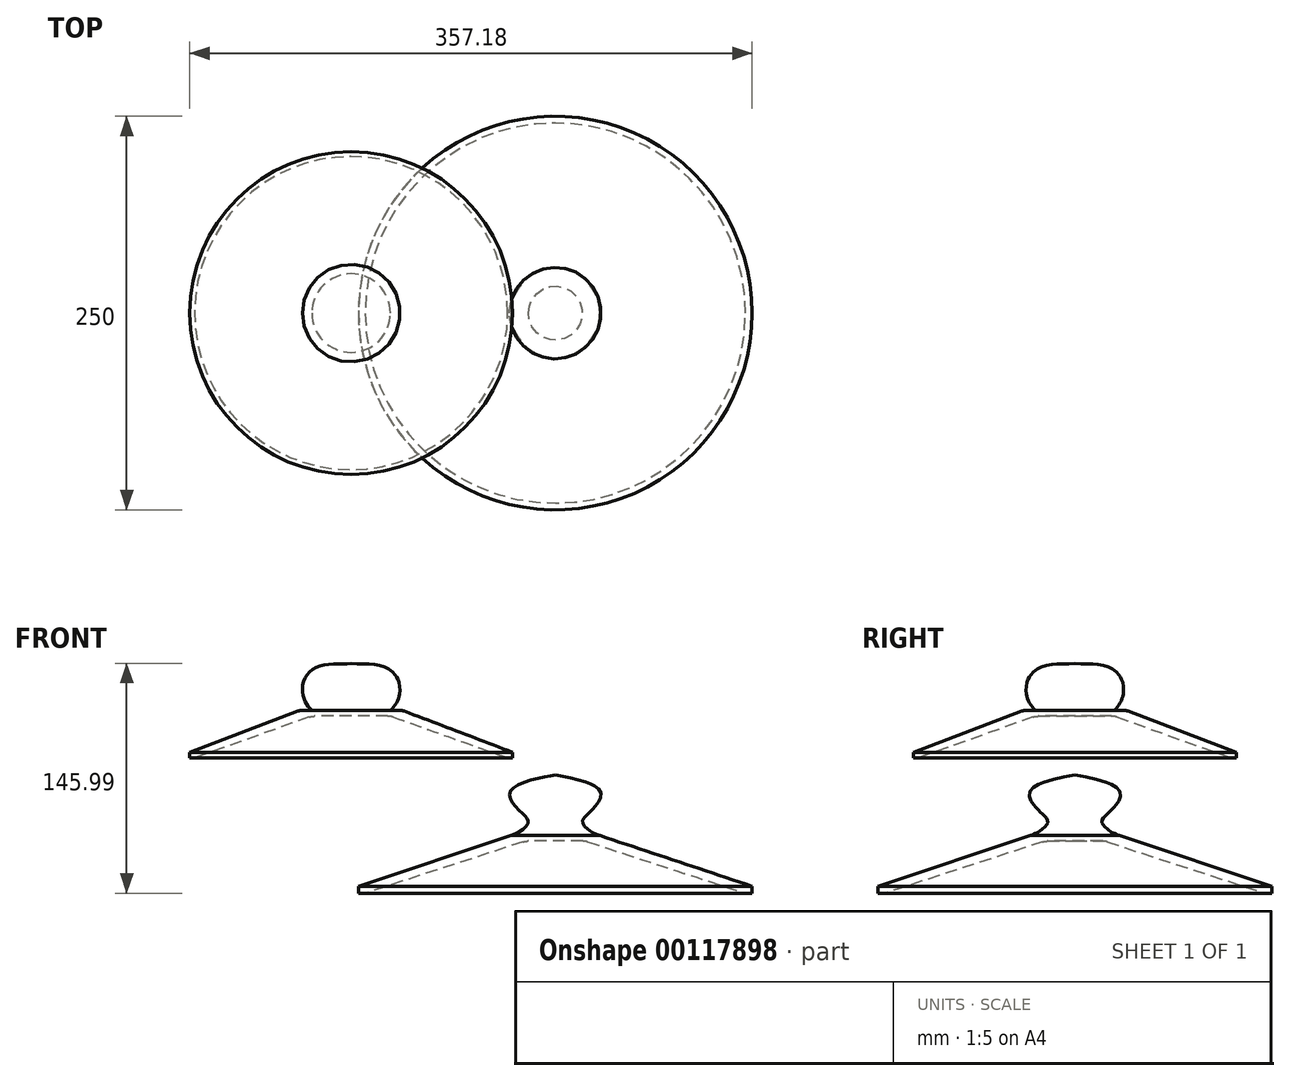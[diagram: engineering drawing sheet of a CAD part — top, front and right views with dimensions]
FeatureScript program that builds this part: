
annotation { "Feature Type Name" : "Feature", "Feature Type Description" : "" }
export const myFeature = defineFeature(function(context is Context, id is Id, definition is map)
    precondition{}
    {
        {
            var Q0;
            Q0=qCreatedBy(makeId("Front.planeOp"),FACE);
            var sketch = newSketch(context, id + "F0", { "sketchPlane" : qUnion([Q0])});
            skLineSegment(sketch, "E0.bottom", {"start": v(-58.02, 56.21) * mm, "end": v(44.48, 56.21) * mm});
            skLineSegment(sketch, "E0.top", {"start": v(-58.02, -3.79) * mm, "end": v(-54.94, -3.79) * mm});
            skLineSegment(sketch, "E0.left", {"start": v(-58.02, 56.21) * mm, "end": v(-58.02, 27.98) * mm});
            skLineSegment(sketch, "E0.right", {"start": v(44.48, 56.21) * mm, "end": v(44.48, 26.21) * mm});
            skLineSegment(sketch, "E1", {"start": v(-58.02, -0.25) * mm, "end": v(-58.02, -3.79) * mm});
            skLineSegment(sketch, "E2", {"start": v(-58.02, -0.25) * mm, "end": v(10.73, 25.88) * mm});
            skLineSegment(sketch, "E3", {"start": v(-54.94, -3.79) * mm, "end": v(44.48, -3.79) * mm});
            skLineSegment(sketch, "E4", {"start": v(-58.02, 27.98) * mm, "end": v(-58.02, -0.25) * mm});
            skLineSegment(sketch, "E5", {"start": v(44.48, 26.21) * mm, "end": v(44.48, 22.67) * mm});
            skLineSegment(sketch, "E6", {"start": v(44.48, 22.67) * mm, "end": v(44.48, -3.79) * mm});
            skLineSegment(sketch, "E7", {"start": v(12.5, 26.21) * mm, "end": v(19.51, 26.21) * mm});
            skLineSegment(sketch, "E8", {"start": v(44.48, 22.67) * mm, "end": v(21.24, 22.67) * mm});
            skLineSegment(sketch, "E9", {"start": v(17.89, 22.1) * mm, "end": v(-54.94, -3.79) * mm});
            skPoint(sketch, "E10.visualSharp", {"position": v(11.59, 26.21) * mm});
            skArc(sketch, "E10.filletArc", {"start": v(12.5, 26.21) * mm, "mid": v(11.6, 26.13) * mm, "end": v(10.73, 25.88) * mm});
            skPoint(sketch, "E11.visualSharp", {"position": v(19.51, 22.67) * mm});
            skArc(sketch, "E11.filletArc", {"start": v(21.24, 22.67) * mm, "mid": v(19.54, 22.53) * mm, "end": v(17.89, 22.1) * mm});
            skFitSpline(sketch, "E12", {"points": [v(19.51, 26.21) * mm, v(14.8, 32.98) * mm, v(14.28, 44.66) * mm, v(24.38, 54.5) * mm, v(44.48, 56.21) * mm], "startDerivative": vector(-25.82, 29.33) * mm, "endDerivative": vector(55.7, 7.93) * mm});
            skLineSegment(sketch, "E13.bottom", {"start": v(49.16, -14.78) * mm, "end": v(174.16, -14.78) * mm});
            skLineSegment(sketch, "E13.top", {"start": v(49.16, -89.78) * mm, "end": v(53.43, -89.78) * mm});
            skLineSegment(sketch, "E13.left", {"start": v(49.16, -14.78) * mm, "end": v(49.16, -50.08) * mm});
            skLineSegment(sketch, "E13.right", {"start": v(174.16, -14.78) * mm, "end": v(174.16, -52.28) * mm});
            skLineSegment(sketch, "E14", {"start": v(49.16, -85.37) * mm, "end": v(49.16, -89.78) * mm});
            skLineSegment(sketch, "E15", {"start": v(53.43, -89.78) * mm, "end": v(174.16, -89.78) * mm});
            skLineSegment(sketch, "E16", {"start": v(49.16, -50.08) * mm, "end": v(49.16, -85.37) * mm});
            skLineSegment(sketch, "E17", {"start": v(174.16, -52.28) * mm, "end": v(174.16, -56.7) * mm});
            skLineSegment(sketch, "E18", {"start": v(174.16, -56.7) * mm, "end": v(174.16, -89.78) * mm});
            skLineSegment(sketch, "E19", {"start": v(174.16, -56.7) * mm, "end": v(156.72, -56.7) * mm});
            skLineSegment(sketch, "E20", {"start": v(153.63, -57.19) * mm, "end": v(53.43, -89.78) * mm});
            skPoint(sketch, "E21.visualSharp", {"position": v(155.14, -56.7) * mm});
            skArc(sketch, "E21.filletArc", {"start": v(156.72, -56.7) * mm, "mid": v(155.16, -56.82) * mm, "end": v(153.63, -57.19) * mm});
            skFitSpline(sketch, "E22", {"points": [v(145.9, -53.15) * mm, v(156.91, -44.98) * mm, v(152.05, -38.02) * mm, v(145.8, -24.66) * mm, v(174.16, -14.78) * mm], "startDerivative": vector(58.9, 16.83) * mm, "endDerivative": vector(55.7, 7.93) * mm});
            skLineSegment(sketch, "E23", {"start": v(49.16, -85.37) * mm, "end": v(145.9, -53.15) * mm});
            skSolve(sketch);
        }
        {
            var Q0;
            Q0=makeQuery(id+"F0.imprint","IMPRINT",FACE,{"disambiguationData":[TD([[makeQuery(id+"F0.imprint","IMPRINT",EDGE,{"derivedFrom":sQuery(id+"F0.wireOp",EDGE,"E0.top")}),1.0]])]});
            var Q1;
            Q1=sQuery(id+"F0.wireOp",EDGE,"E0.right");
            revolve(context, id + "F1", {"entities" : qUnion([Q0]), "axis" : qUnion([Q1]), "revolveType" : RevolveType.FULL});
        }
        {
            var Q0;
            Q0=makeQuery(id+"F0.imprint","IMPRINT",FACE,{"disambiguationData":[TD([[makeQuery(id+"F0.imprint","IMPRINT",EDGE,{"derivedFrom":sQuery(id+"F0.wireOp",EDGE,"E13.top")}),1.0]])]});
            var Q1;
            Q1=sQuery(id+"F0.wireOp",EDGE,"E13.right");
            revolve(context, id + "F2", {"entities" : qUnion([Q0]), "axis" : qUnion([Q1]), "revolveType" : RevolveType.FULL});
        }
    });
